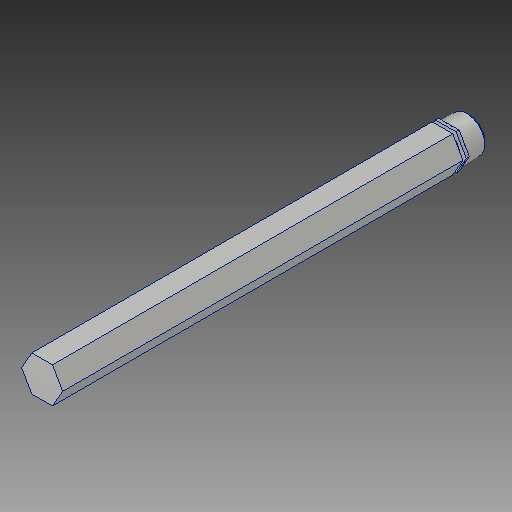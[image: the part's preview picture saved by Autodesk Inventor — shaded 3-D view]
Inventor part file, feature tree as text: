
AUTODESK INVENTOR PART (.ipt)
format: ipt  version: 2017 (Build 210142000, 142)  size: 90,624 bytes
history: native  units: in
note: dims shown in document units (in); Inventor stores cm internally (conversion verified against a paired STEP export)
features: chamfer x1
ambient origin geometry x8: Origin, YZ Plane, XZ Plane, XY Plane, X Axis, Y Axis, Z Axis, Center Point
bodies: Solid1 (feature_tree)
feature tree (1):
  chamfer  "Chamfer1"  [1 undecoded]
note: 1 required parameter value undecoded (feature->parameter linkage not recoverable at this tier; creation-order binding heuristic only, values carry confidence <= 0.55)
